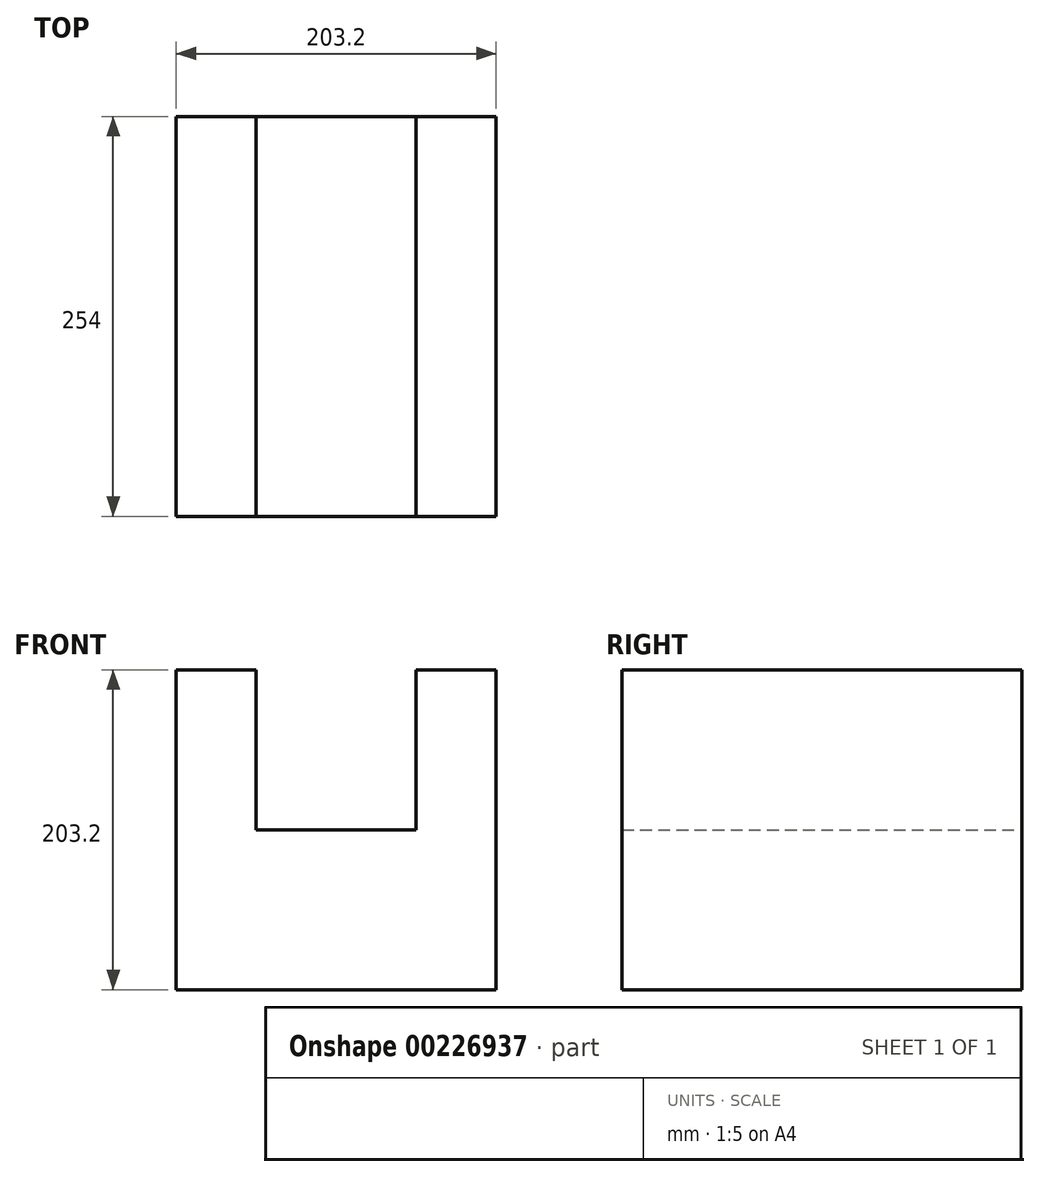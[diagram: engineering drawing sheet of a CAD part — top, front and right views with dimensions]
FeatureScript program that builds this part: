
annotation { "Feature Type Name" : "Feature", "Feature Type Description" : "" }
export const myFeature = defineFeature(function(context is Context, id is Id, definition is map)
    precondition{}
    {
        {
            var Q0;
            Q0=qCreatedBy(makeId("Front.planeOp"),FACE);
            var sketch = newSketch(context, id + "F0", { "sketchPlane" : qUnion([Q0])});
            skLineSegment(sketch, "E0.top", {"start": v(-139.06, -103.4) * mm, "end": v(64.14, -103.4) * mm});
            skLineSegment(sketch, "E0.left", {"start": v(-139.06, 99.8) * mm, "end": v(-139.06, -103.4) * mm});
            skLineSegment(sketch, "E0.right", {"start": v(64.14, 99.8) * mm, "end": v(64.14, -103.4) * mm});
            skLineSegment(sketch, "E1", {"start": v(-88.26, 99.8) * mm, "end": v(-88.26, -1.8) * mm});
            skLineSegment(sketch, "E2", {"start": v(-88.26, -1.8) * mm, "end": v(13.34, -1.8) * mm});
            skLineSegment(sketch, "E3", {"start": v(13.34, -1.8) * mm, "end": v(13.34, 99.8) * mm});
            skLineSegment(sketch, "E4", {"start": v(-139.06, 99.8) * mm, "end": v(-88.26, 99.8) * mm});
            skLineSegment(sketch, "E5", {"start": v(13.34, 99.8) * mm, "end": v(64.14, 99.8) * mm});
            skSolve(sketch);
        }
        {
            var Q0;
            Q0=makeQuery(id+"F0.imprint","IMPRINT",FACE,{"disambiguationData":[TD([[makeQuery(id+"F0.imprint","IMPRINT",EDGE,{"derivedFrom":sQuery(id+"F0.wireOp",EDGE,"E0.top")}),1.0]])]});
            extrude(context, id + "F1", {"entities" : qUnion([Q0]), "depth" : 254 * mm});
        }
    });
